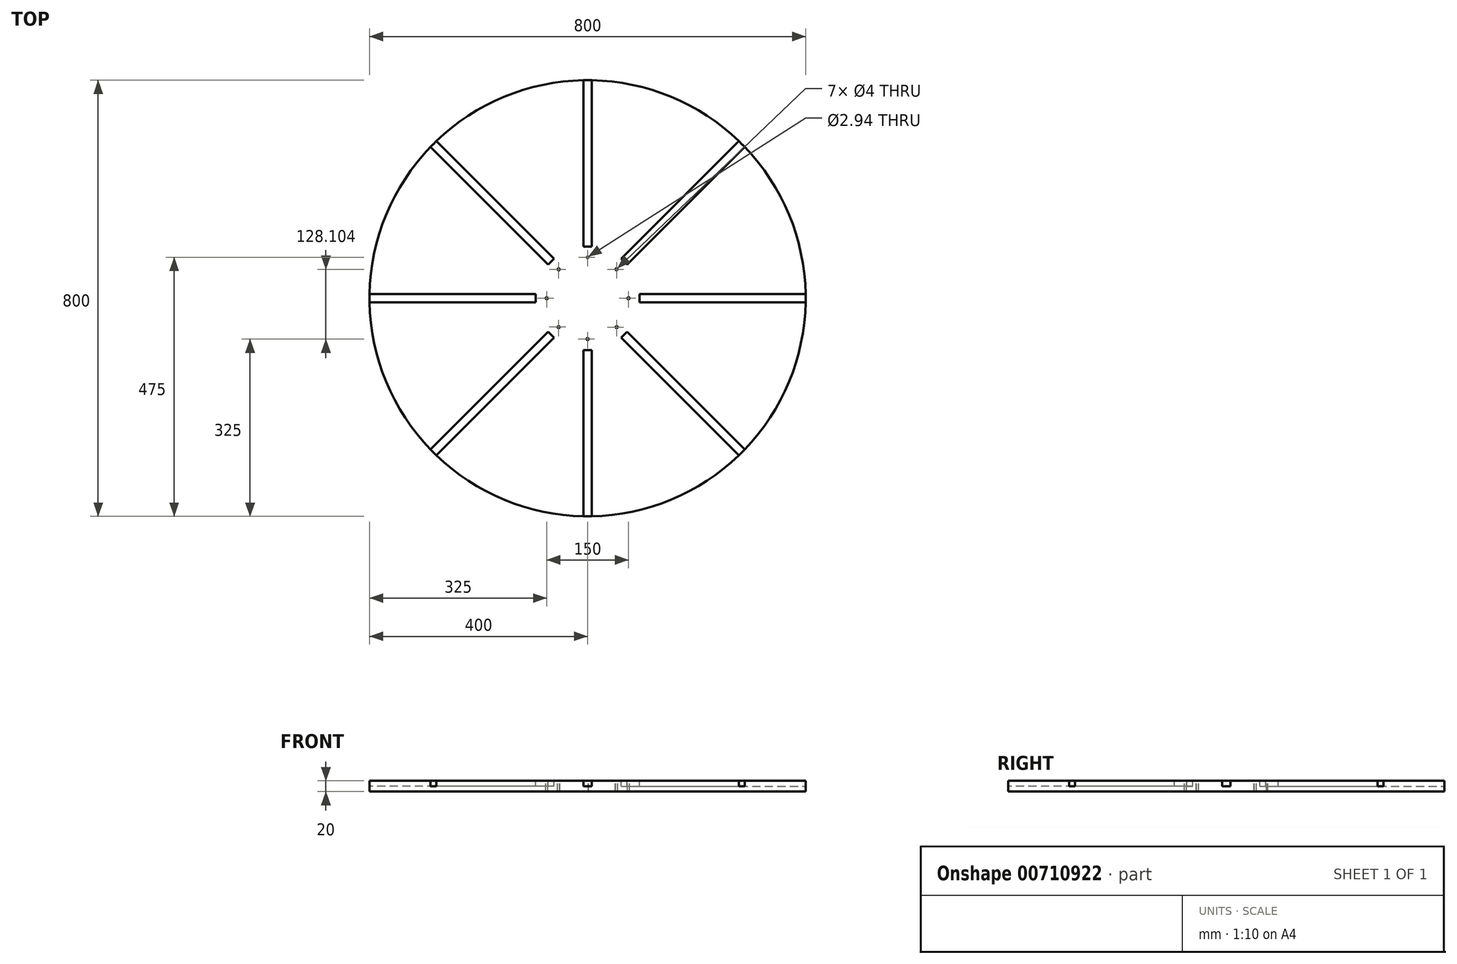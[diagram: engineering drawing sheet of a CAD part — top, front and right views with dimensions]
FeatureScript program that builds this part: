
annotation { "Feature Type Name" : "Feature", "Feature Type Description" : "" }
export const myFeature = defineFeature(function(context is Context, id is Id, definition is map)
    precondition{}
    {
        {
            var Q0;
            Q0=qCreatedBy(makeId("Top.planeOp"),FACE);
            var sketch = newSketch(context, id + "F0", { "sketchPlane" : qUnion([Q0])});
            skCircle(sketch, "E0", {"center": v(0, 0) * mm, "radius": 400 * mm});
            skSolve(sketch);
        }
        {
            var Q0;
            Q0=makeQuery(id+"F0.imprint","IMPRINT",FACE,{"disambiguationData":[TD([[makeQuery(id+"F0.imprint","IMPRINT",EDGE,{"derivedFrom":sQuery(id+"F0.wireOp",EDGE,"E0")}),1.0]])]});
            extrude(context, id + "F1", {"entities" : qUnion([Q0]), "oppositeDirection" : true, "depth" : 20 * mm, "offsetDistance" : 25 * mm});
        }
        {
            var Q0;
            Q0=makeQuery(id+"F1.opExtrude","CAP_FACE",FACE,{"disambiguationData":[OSD([sQuery(id+"F0.wireOp",EDGE,"E0")])],"isStart":true});
            var sketch = newSketch(context, id + "F2", { "sketchPlane" : qUnion([Q0])});
            skLineSegment(sketch, "E1", {"start": v(0, 0) * mm, "end": v(0, -400) * mm, "construction": true});
            skLineSegment(sketch, "E2.1.0", {"start": v(0, 0) * mm, "end": v(282.84, -282.84) * mm, "construction": true});
            skLineSegment(sketch, "E2.2.0", {"start": v(0, 0) * mm, "end": v(400, 0) * mm, "construction": true});
            skLineSegment(sketch, "E2.3.0", {"start": v(0, 0) * mm, "end": v(282.84, 282.84) * mm, "construction": true});
            skLineSegment(sketch, "E2.4.0", {"start": v(0, 0) * mm, "end": v(0, 400) * mm, "construction": true});
            skLineSegment(sketch, "E2.5.0", {"start": v(0, 0) * mm, "end": v(-282.84, 282.84) * mm, "construction": true});
            skLineSegment(sketch, "E2.6.0", {"start": v(0, 0) * mm, "end": v(-400, 0) * mm, "construction": true});
            skLineSegment(sketch, "E2.7.0", {"start": v(0, 0) * mm, "end": v(-282.84, -282.84) * mm, "construction": true});
            skPoint(sketch, "E2.center", {"position": v(0, 0) * mm});
            skSolve(sketch);
        }
        {
            var Q0;
            Q0=qCreatedBy(makeId("Top.planeOp"),FACE);
            var sketch = newSketch(context, id + "F3", { "sketchPlane" : qUnion([Q0])});
            skCircle(sketch, "E3", {"center": v(0, 0) * mm, "radius": 75 * mm, "construction": true});
            skCircle(sketch, "E4", {"center": v(-75, 0) * mm, "radius": 2 * mm});
            skCircle(sketch, "E5.1.0", {"center": v(-53.03, -53.03) * mm, "radius": 2 * mm});
            skCircle(sketch, "E5.2.0", {"center": v(0, -75) * mm, "radius": 2 * mm});
            skCircle(sketch, "E5.3.0", {"center": v(53.03, -53.03) * mm, "radius": 2 * mm});
            skCircle(sketch, "E5.4.0", {"center": v(75, 0) * mm, "radius": 2 * mm});
            skCircle(sketch, "E5.5.0", {"center": v(53.03, 53.03) * mm, "radius": 2 * mm});
            skCircle(sketch, "E5.6.0", {"center": v(0, 75) * mm, "radius": 2 * mm});
            skCircle(sketch, "E5.7.0", {"center": v(-53.03, 53.03) * mm, "radius": 2 * mm});
            skSolve(sketch);
        }
        {
            var Q0;
            Q0=makeQuery(id+"F3.imprint","IMPRINT",FACE,{"disambiguationData":[TD([[makeQuery(id+"F3.imprint","IMPRINT",EDGE,{"derivedFrom":sQuery(id+"F3.wireOp",EDGE,"E4")}),1.0]])]});
            extrude(context, id + "F4", {"entities" : qUnion([Q0]), "operationType" : NewBodyOperationType.REMOVE, "oppositeDirection" : true, "depth" : 20 * mm, "offsetDistance" : 25 * mm});
        }
        {
            var Q0;
            Q0=qCreatedBy(makeId("Top.planeOp"),FACE);
            var sketch = newSketch(context, id + "F5", { "sketchPlane" : qUnion([Q0])});
            skCircle(sketch, "E6", {"center": v(0, 0) * mm, "radius": 75 * mm, "construction": true});
            skCircle(sketch, "E7", {"center": v(-53.16, -52.9) * mm, "radius": 2 * mm});
            skSolve(sketch);
        }
        {
            var Q0;
            Q0 = qSketchRegion(id + "F5", true);
            extrude(context, id + "F6", {"entities" : qUnion([Q0]), "operationType" : NewBodyOperationType.REMOVE, "oppositeDirection" : true, "depth" : 20 * mm, "offsetDistance" : 25 * mm});
        }
        {
            var Q0;
            Q0=makeQuery(id+"F2.imprint","IMPRINT",FACE,{"disambiguationData":[TD([[makeQuery(id+"F2.imprint","IMPRINT",EDGE,{"derivedFrom":makeQuery(id+"F1.opExtrude","CAP_EDGE",EDGE,{"disambiguationData":[OSD([sQuery(id+"F0.wireOp",EDGE,"E0")])],"isStart":true})}),1.0]])]});
            cPlane(context, id + "F7", {"entities" : qUnion([Q0]), "cplaneType" : CPlaneType.OFFSET, "offset" : 0 * mm, "width" : 150 * mm, "height" : 150 * mm});
        }
        {
            var Q0;
            Q0=qCreatedBy(id+"F7.planeOp",FACE);
            var sketch = newSketch(context, id + "F8", { "sketchPlane" : qUnion([Q0])});
            skCircle(sketch, "E8", {"center": v(0, -75) * mm, "radius": 2 * mm});
            skSolve(sketch);
        }
        {
            var Q0;
            Q0 = qSketchRegion(id + "F8", true);
            extrude(context, id + "F9", {"entities" : qUnion([Q0]), "operationType" : NewBodyOperationType.REMOVE, "oppositeDirection" : true, "depth" : 20 * mm, "offsetDistance" : 25 * mm});
        }
        {
            var Q0;
            Q0=qCreatedBy(id+"F7.planeOp",FACE);
            var sketch = newSketch(context, id + "F10", { "sketchPlane" : qUnion([Q0])});
            skCircle(sketch, "E9", {"center": v(53.37, -52.97) * mm, "radius": 2 * mm});
            skSolve(sketch);
        }
        {
            var Q0;
            Q0 = qSketchRegion(id + "F10", true);
            extrude(context, id + "F11", {"entities" : qUnion([Q0]), "operationType" : NewBodyOperationType.REMOVE, "oppositeDirection" : true, "depth" : 20 * mm, "offsetDistance" : 25 * mm});
        }
        {
            var Q0;
            Q0=qCreatedBy(id+"F7.planeOp",FACE);
            var sketch = newSketch(context, id + "F12", { "sketchPlane" : qUnion([Q0])});
            skCircle(sketch, "E10", {"center": v(75, 0) * mm, "radius": 2 * mm});
            skSolve(sketch);
        }
        {
            var Q0;
            Q0=makeQuery(id+"F12.imprint","IMPRINT",FACE,{"disambiguationData":[TD([[makeQuery(id+"F12.imprint","IMPRINT",EDGE,{"derivedFrom":sQuery(id+"F12.wireOp",EDGE,"E10")}),1.0]])]});
            extrude(context, id + "F13", {"entities" : qUnion([Q0]), "operationType" : NewBodyOperationType.REMOVE, "oppositeDirection" : true, "depth" : 20 * mm, "offsetDistance" : 25 * mm});
        }
        {
            var Q0;
            Q0=qCreatedBy(id+"F7.planeOp",FACE);
            var sketch = newSketch(context, id + "F14", { "sketchPlane" : qUnion([Q0])});
            skCircle(sketch, "E11", {"center": v(53.1, 53.1) * mm, "radius": 2 * mm});
            skSolve(sketch);
        }
        {
            var Q0;
            Q0=makeQuery(id+"F14.imprint","IMPRINT",FACE,{"disambiguationData":[TD([[makeQuery(id+"F14.imprint","IMPRINT",EDGE,{"derivedFrom":sQuery(id+"F14.wireOp",EDGE,"E11")}),1.0]])]});
            extrude(context, id + "F15", {"entities" : qUnion([Q0]), "operationType" : NewBodyOperationType.REMOVE, "oppositeDirection" : true, "depth" : 20 * mm, "offsetDistance" : 25 * mm});
        }
        {
            var Q0;
            Q0=qCreatedBy(id+"F7.planeOp",FACE);
            var sketch = newSketch(context, id + "F16", { "sketchPlane" : qUnion([Q0])});
            skCircle(sketch, "E12", {"center": v(0, 75) * mm, "radius": 1.47 * mm});
            skCircle(sketch, "E13", {"center": v(-53.04, 53.03) * mm, "radius": 2 * mm});
            skSolve(sketch);
        }
        {
            var Q0;
            Q0=makeQuery(id+"F16.imprint","IMPRINT",FACE,{"disambiguationData":[TD([[makeQuery(id+"F16.imprint","IMPRINT",EDGE,{"derivedFrom":sQuery(id+"F16.wireOp",EDGE,"E12")}),1.0]])]});
            extrude(context, id + "F17", {"entities" : qUnion([Q0]), "operationType" : NewBodyOperationType.REMOVE, "oppositeDirection" : true, "depth" : 20 * mm, "offsetDistance" : 25 * mm});
        }
        {
            var Q0;
            Q0=qCreatedBy(id+"F7.planeOp",FACE);
            var sketch = newSketch(context, id + "F18", { "sketchPlane" : qUnion([Q0])});
            skCircle(sketch, "E14", {"center": v(-53.06, 53.05) * mm, "radius": 2 * mm});
            skSolve(sketch);
        }
        {
            var Q0;
            Q0=makeQuery(id+"F18.imprint","IMPRINT",FACE,{"disambiguationData":[TD([[makeQuery(id+"F18.imprint","IMPRINT",EDGE,{"derivedFrom":sQuery(id+"F18.wireOp",EDGE,"E14")}),1.0]])]});
            extrude(context, id + "F19", {"entities" : qUnion([Q0]), "operationType" : NewBodyOperationType.REMOVE, "oppositeDirection" : true, "depth" : 20 * mm, "offsetDistance" : 25 * mm});
        }
        {
            var Q0;
            Q0=qCreatedBy(id+"F7.planeOp",FACE);
            var sketch = newSketch(context, id + "F20", { "sketchPlane" : qUnion([Q0])});
            skLineSegment(sketch, "E15.bottom", {"start": v(-7.65, -95) * mm, "end": v(7.65, -95) * mm});
            skLineSegment(sketch, "E15.top", {"start": v(-7.65, -400) * mm, "end": v(7.65, -400) * mm});
            skLineSegment(sketch, "E15.left", {"start": v(-7.65, -95) * mm, "end": v(-7.65, -400) * mm});
            skLineSegment(sketch, "E15.right", {"start": v(7.65, -95) * mm, "end": v(7.65, -400) * mm});
            skPoint(sketch, "E15.middle", {"position": v(0, -247.5) * mm});
            skPoint(sketch, "E16.1.0", {"position": v(175, -175) * mm});
            skLineSegment(sketch, "E16.1.1", {"start": v(72.58, -61.77) * mm, "end": v(288.25, -277.44) * mm});
            skLineSegment(sketch, "E16.1.2", {"start": v(61.77, -72.58) * mm, "end": v(277.44, -288.25) * mm});
            skLineSegment(sketch, "E16.1.3", {"start": v(277.44, -288.25) * mm, "end": v(288.25, -277.44) * mm});
            skLineSegment(sketch, "E16.1.4", {"start": v(61.77, -72.58) * mm, "end": v(72.58, -61.77) * mm});
            skPoint(sketch, "E16.2.0", {"position": v(247.5, 0) * mm});
            skLineSegment(sketch, "E16.2.1", {"start": v(95, 7.65) * mm, "end": v(400, 7.65) * mm});
            skLineSegment(sketch, "E16.2.2", {"start": v(95, -7.65) * mm, "end": v(400, -7.65) * mm});
            skLineSegment(sketch, "E16.2.3", {"start": v(400, -7.65) * mm, "end": v(400, 7.65) * mm});
            skLineSegment(sketch, "E16.2.4", {"start": v(95, -7.65) * mm, "end": v(95, 7.65) * mm});
            skPoint(sketch, "E16.3.0", {"position": v(175, 175) * mm});
            skLineSegment(sketch, "E16.3.1", {"start": v(61.77, 72.58) * mm, "end": v(277.44, 288.25) * mm});
            skLineSegment(sketch, "E16.3.2", {"start": v(72.58, 61.77) * mm, "end": v(288.25, 277.44) * mm});
            skLineSegment(sketch, "E16.3.3", {"start": v(288.25, 277.44) * mm, "end": v(277.44, 288.25) * mm});
            skLineSegment(sketch, "E16.3.4", {"start": v(72.58, 61.77) * mm, "end": v(61.77, 72.58) * mm});
            skPoint(sketch, "E16.4.0", {"position": v(0, 247.5) * mm});
            skLineSegment(sketch, "E16.4.1", {"start": v(-7.65, 95) * mm, "end": v(-7.65, 400) * mm});
            skLineSegment(sketch, "E16.4.2", {"start": v(7.65, 95) * mm, "end": v(7.65, 400) * mm});
            skLineSegment(sketch, "E16.4.3", {"start": v(7.65, 400) * mm, "end": v(-7.65, 400) * mm});
            skLineSegment(sketch, "E16.4.4", {"start": v(7.65, 95) * mm, "end": v(-7.65, 95) * mm});
            skPoint(sketch, "E16.5.0", {"position": v(-175, 175) * mm});
            skLineSegment(sketch, "E16.5.1", {"start": v(-72.58, 61.77) * mm, "end": v(-288.25, 277.44) * mm});
            skLineSegment(sketch, "E16.5.2", {"start": v(-61.77, 72.58) * mm, "end": v(-277.44, 288.25) * mm});
            skLineSegment(sketch, "E16.5.3", {"start": v(-277.44, 288.25) * mm, "end": v(-288.25, 277.44) * mm});
            skLineSegment(sketch, "E16.5.4", {"start": v(-61.77, 72.58) * mm, "end": v(-72.58, 61.77) * mm});
            skPoint(sketch, "E16.6.0", {"position": v(-247.5, 0) * mm});
            skLineSegment(sketch, "E16.6.1", {"start": v(-95, -7.65) * mm, "end": v(-400, -7.65) * mm});
            skLineSegment(sketch, "E16.6.2", {"start": v(-95, 7.65) * mm, "end": v(-400, 7.65) * mm});
            skLineSegment(sketch, "E16.6.3", {"start": v(-400, 7.65) * mm, "end": v(-400, -7.65) * mm});
            skLineSegment(sketch, "E16.6.4", {"start": v(-95, 7.65) * mm, "end": v(-95, -7.65) * mm});
            skPoint(sketch, "E16.7.0", {"position": v(-175, -175) * mm});
            skLineSegment(sketch, "E16.7.1", {"start": v(-61.77, -72.58) * mm, "end": v(-277.44, -288.25) * mm});
            skLineSegment(sketch, "E16.7.2", {"start": v(-72.58, -61.77) * mm, "end": v(-288.25, -277.44) * mm});
            skLineSegment(sketch, "E16.7.3", {"start": v(-288.25, -277.44) * mm, "end": v(-277.44, -288.25) * mm});
            skLineSegment(sketch, "E16.7.4", {"start": v(-72.58, -61.77) * mm, "end": v(-61.77, -72.58) * mm});
            skPoint(sketch, "E16.center", {"position": v(0, 0) * mm});
            skSolve(sketch);
        }
        {
            var Q0;
            Q0 = qSketchRegion(id + "F20", true);
            extrude(context, id + "F21", {"entities" : qUnion([Q0]), "operationType" : NewBodyOperationType.REMOVE, "oppositeDirection" : true, "depth" : 10 * mm, "offsetDistance" : 25 * mm});
        }
    });
